# Revit family: PF 19
name_source: partatom
category: Lighting Fixtures
units: mm (PartAtom-declared; Revit-internal decimal feet)

## family parameters
Cut with Voids When Loaded = No
Host = Face
Light Source = Yes
OmniClass Number = 23.80.70.11
OmniClass Title = Luminaries for Internal Lighting
Part Type = Normal
Room Calculation Point = No
Round Connector Dimension = Use Diameter
Shared = No

## types (2) — shared parameters
Beam angle (°) = 110°
CRI L'indice di Resa Cromatica = 85
Color Filter = 16777215
Description = Plafoniera espressamente progettata per ospitare nuove fonti luminose LED COB ad alta efficienza. Il profilo sottile ma strutturalmente incisivo della PF 19 si inserisce con naturalezza in ogni ambiente, soprattutto in spazi con altezze ridotte, sia in ambienti pubblici sia in residenze private.
Dimming Lamp Color Temperature Shift = <None>
Effective Intensity (lm) = 1152
Glass material = Glass
Lamp = LED 1800lm 12W 3000K CRI85
Larghezza = 190 mm
Manufacturer = ARIA
Photometric Web File = 3880-01 _ PF 19 LED 12W 1800 lm 120°.IES
Tilt Angle = 90.00°
Type Comments = Ceiling / Wall light
URL = https://www.aria.lighting
Wattage Comments = 12

## per-type parameters (varying)
| type | Body material | Codice | Model | Type Image |
| PF 19 1800lm 12W 3000K CRI85-110°- WHITE | White Powder Coated Aluminium | 3881-01-21 | 3881-01-21 | PF 19 ARIA.jpg |
| PF 19 1800lm 12W 3000K CRI85-110°- METAL | Aluminum | 3881-01-52 | 3881-01-52 | PF 19 ARIA METAL.jpg |

## geometry (parser evidence)
native form markers: Sweep x3
no freeform markers — native parametric forms only
